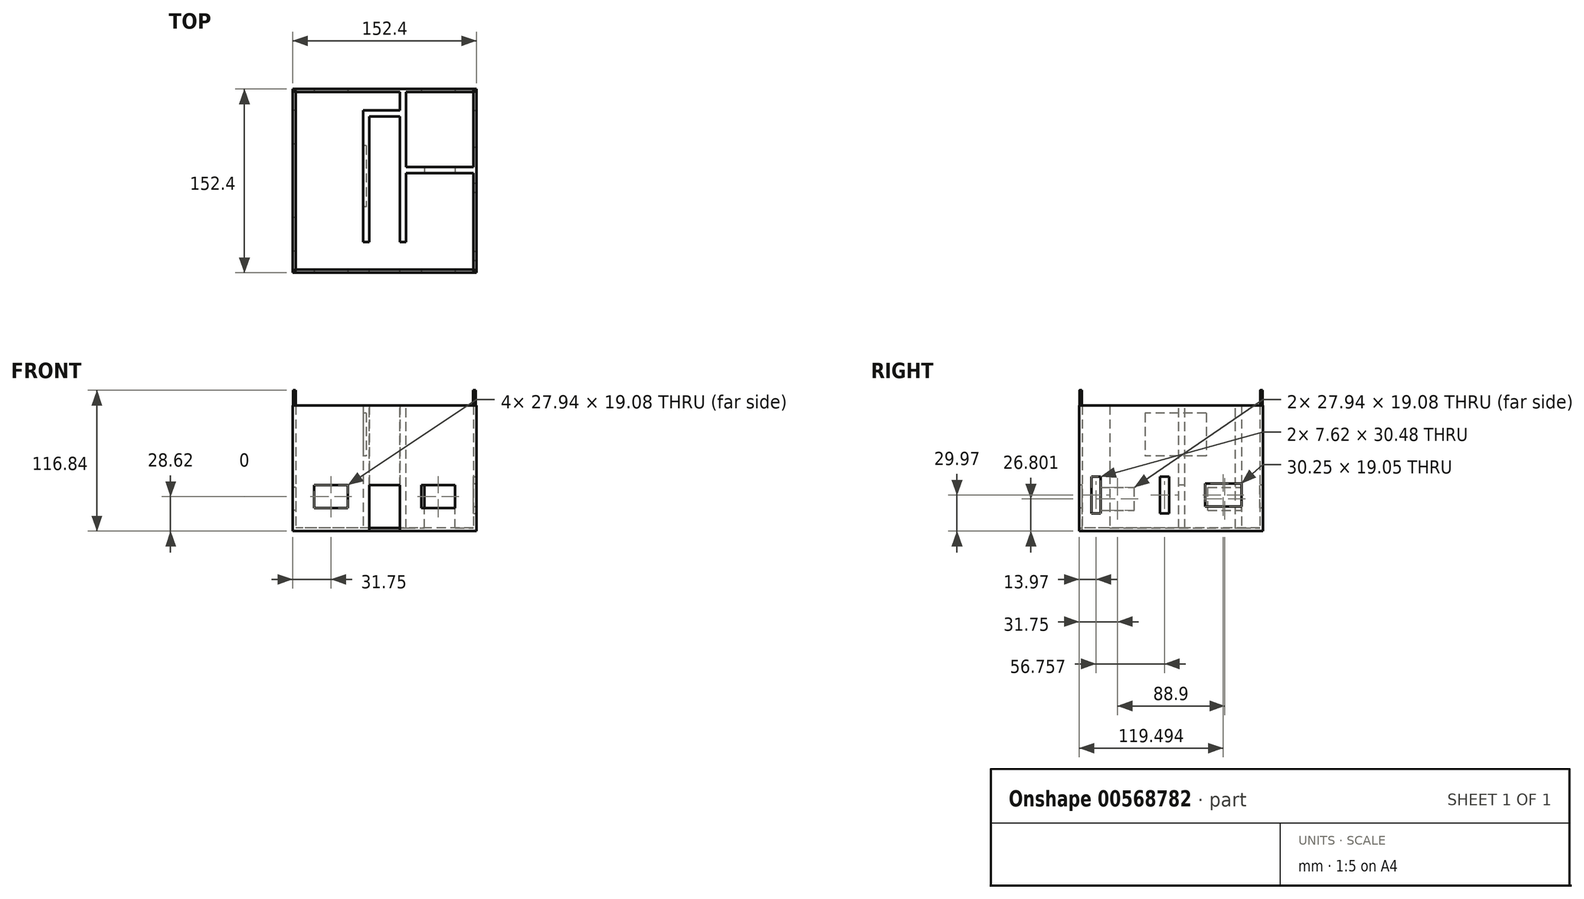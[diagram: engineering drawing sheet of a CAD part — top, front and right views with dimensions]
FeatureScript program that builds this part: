
annotation { "Feature Type Name" : "Feature", "Feature Type Description" : "" }
export const myFeature = defineFeature(function(context is Context, id is Id, definition is map)
    precondition{}
    {
        {
            var Q0;
            Q0=qCreatedBy(makeId("Top.planeOp"),FACE);
            var sketch = newSketch(context, id + "F0", { "sketchPlane" : qUnion([Q0])});
            skLineSegment(sketch, "E0.bottom", {"start": v(0, 0) * mm, "end": v(152.4, 0) * mm});
            skLineSegment(sketch, "E0.top", {"start": v(0, -152.4) * mm, "end": v(152.4, -152.4) * mm});
            skLineSegment(sketch, "E0.left", {"start": v(0, 0) * mm, "end": v(0, -152.4) * mm});
            skLineSegment(sketch, "E0.right", {"start": v(152.4, 0) * mm, "end": v(152.4, -152.4) * mm});
            skSolve(sketch);
        }
        {
            var Q0;
            Q0 = qSketchRegion(id + "F0", true);
            extrude(context, id + "F1", {"entities" : qUnion([Q0]), "depth" : 2.54 * mm, "offsetDistance" : 25.4 * mm});
        }
        {
            var Q0;
            Q0=makeQuery(id+"F1.opExtrude","CAP_FACE",FACE,{"disambiguationData":[OSD([sQuery(id+"F0.wireOp",EDGE,"E0.bottom"),sQuery(id+"F0.wireOp",EDGE,"E0.top"),sQuery(id+"F0.wireOp",EDGE,"E0.left"),sQuery(id+"F0.wireOp",EDGE,"E0.right")])],"isStart":false});
            var sketch = newSketch(context, id + "F2", { "sketchPlane" : qUnion([Q0])});
            skLineSegment(sketch, "E1", {"start": v(76.2, 0) * mm, "end": v(76.2, -152.4) * mm, "construction": true});
            skLineSegment(sketch, "E2", {"start": v(76.2, -152.4) * mm, "end": v(0, -76.2) * mm, "construction": true});
            skLineSegment(sketch, "E3", {"start": v(0, -76.2) * mm, "end": v(152.4, -76.2) * mm, "construction": true});
            skLineSegment(sketch, "E4", {"start": v(152.4, -76.2) * mm, "end": v(76.2, 0) * mm, "construction": true});
            skLineSegment(sketch, "E5.bottom", {"start": v(149.86, -2.54) * mm, "end": v(2.54, -2.54) * mm});
            skLineSegment(sketch, "E5.top", {"start": v(149.86, -149.86) * mm, "end": v(2.54, -149.86) * mm});
            skLineSegment(sketch, "E5.left", {"start": v(149.86, -2.54) * mm, "end": v(149.86, -149.86) * mm});
            skLineSegment(sketch, "E5.right", {"start": v(2.54, -2.54) * mm, "end": v(2.54, -149.86) * mm});
            skSolve(sketch);
        }
        {
            var Q0;
            Q0=makeQuery(id+"F2.imprint","IMPRINT",FACE,{"disambiguationData":[TD([[makeQuery(id+"F2.imprint","IMPRINT",EDGE,{"derivedFrom":sQuery(id+"F2.wireOp",EDGE,"E5.bottom")}),-1.0]])]});
            extrude(context, id + "F3", {"entities" : qUnion([Q0]), "operationType" : NewBodyOperationType.ADD, "depth" : 101.6 * mm, "offsetDistance" : 25.4 * mm});
        }
        {
            var Q0;
            {var subQ0=sQuery(id+"F0.wireOp",EDGE,"E0.top");Q0=makeQuery(id+"F3.boolean.opBoolean","MERGE",FACE,{"derivedFrom":[makeQuery(id+"F1.opExtrude","SWEPT_FACE",FACE,{"disambiguationData":[OSD([subQ0])]}),makeQuery(id+"F3.opExtrude","SWEPT_FACE",FACE,{"disambiguationData":[OSD([subQ0])]})]});}
            var sketch = newSketch(context, id + "F4", { "sketchPlane" : qUnion([Q0])});
            skLineSegment(sketch, "E6", {"start": v(76.2, 104.14) * mm, "end": v(76.2, 0) * mm, "construction": true});
            skLineSegment(sketch, "E7", {"start": v(76.2, 0) * mm, "end": v(0, 52.07) * mm, "construction": true});
            skLineSegment(sketch, "E8", {"start": v(0, 52.07) * mm, "end": v(152.4, 52.07) * mm, "construction": true});
            skLineSegment(sketch, "E9", {"start": v(152.4, 52.07) * mm, "end": v(76.2, 104.14) * mm, "construction": true});
            skLineSegment(sketch, "E10", {"start": v(76.2, 0) * mm, "end": v(88.9, 0) * mm, "construction": true});
            skLineSegment(sketch, "E11", {"start": v(76.2, 0) * mm, "end": v(63.5, 0) * mm, "construction": true});
            skLineSegment(sketch, "E12.bottom", {"start": v(63.5, 0) * mm, "end": v(88.9, 0) * mm});
            skLineSegment(sketch, "E12.top", {"start": v(63.5, 38.16) * mm, "end": v(88.9, 38.16) * mm});
            skLineSegment(sketch, "E12.left", {"start": v(63.5, 0) * mm, "end": v(63.5, 38.16) * mm});
            skLineSegment(sketch, "E12.right", {"start": v(88.9, 0) * mm, "end": v(88.9, 38.16) * mm});
            skSolve(sketch);
        }
        {
            var Q0;
            Q0=makeQuery(id+"F4.imprint","IMPRINT",FACE,{"disambiguationData":[TD([[makeQuery(id+"F4.imprint","IMPRINT",EDGE,{"derivedFrom":sQuery(id+"F4.wireOp",EDGE,"E12.bottom")}),1.0]])]});
            extrude(context, id + "F5", {"entities" : qUnion([Q0]), "operationType" : NewBodyOperationType.REMOVE, "oppositeDirection" : true, "depth" : 25.4 * mm, "offsetDistance" : 25.4 * mm});
        }
        {
            var Q0;
            Q0=makeQuery(id+"F1.opExtrude","CAP_FACE",FACE,{"disambiguationData":[OSD([sQuery(id+"F0.wireOp",EDGE,"E0.bottom"),sQuery(id+"F0.wireOp",EDGE,"E0.top"),sQuery(id+"F0.wireOp",EDGE,"E0.left"),sQuery(id+"F0.wireOp",EDGE,"E0.right")])],"isStart":false});
            var sketch = newSketch(context, id + "F6", { "sketchPlane" : qUnion([Q0])});
            skLineSegment(sketch, "E13.bottom", {"start": v(63.5, -127) * mm, "end": v(88.9, -127) * mm});
            skLineSegment(sketch, "E13.top", {"start": v(63.5, -149.86) * mm, "end": v(88.9, -149.86) * mm});
            skLineSegment(sketch, "E13.left", {"start": v(63.5, -127) * mm, "end": v(63.5, -149.86) * mm});
            skLineSegment(sketch, "E13.right", {"start": v(88.9, -127) * mm, "end": v(88.9, -149.86) * mm});
            skSolve(sketch);
        }
        {
            var Q0;
            Q0 = qSketchRegion(id + "F6", true);
            extrude(context, id + "F7", {"entities" : qUnion([Q0]), "oppositeDirection" : true, "depth" : 2.54 * mm, "offsetDistance" : 25.4 * mm});
        }
        {
            var Q0;
            Q0=makeQuery(id+"F7.opExtrude","SWEPT_FACE",FACE,{"disambiguationData":[OSD([sQuery(id+"F6.wireOp",EDGE,"E13.top")])]});
            var sketch = newSketch(context, id + "F8", { "sketchPlane" : qUnion([Q0])});
            skLineSegment(sketch, "E14.bottom", {"start": v(88.9, 0) * mm, "end": v(63.5, 0) * mm});
            skLineSegment(sketch, "E14.top", {"start": v(88.9, 2.54) * mm, "end": v(63.5, 2.54) * mm});
            skLineSegment(sketch, "E14.left", {"start": v(88.9, 0) * mm, "end": v(88.9, 2.54) * mm});
            skLineSegment(sketch, "E14.right", {"start": v(63.5, 0) * mm, "end": v(63.5, 2.54) * mm});
            skSolve(sketch);
        }
        {
            var Q0;
            Q0 = qSketchRegion(id + "F8", true);
            extrude(context, id + "F9", {"entities" : qUnion([Q0]), "depth" : 2.54 * mm, "offsetDistance" : 25.4 * mm});
        }
        {
            var Q0;
            Q0=makeQuery(id+"F1.opExtrude","CAP_FACE",FACE,{"disambiguationData":[OSD([sQuery(id+"F0.wireOp",EDGE,"E0.bottom"),sQuery(id+"F0.wireOp",EDGE,"E0.top"),sQuery(id+"F0.wireOp",EDGE,"E0.left"),sQuery(id+"F0.wireOp",EDGE,"E0.right")])],"isStart":false});
            var sketch = newSketch(context, id + "F10", { "sketchPlane" : qUnion([Q0])});
            skLineSegment(sketch, "E15.bottom", {"start": v(63.5, -127) * mm, "end": v(58.42, -127) * mm});
            skLineSegment(sketch, "E15.top", {"start": v(63.5, -17.78) * mm, "end": v(58.42, -17.78) * mm});
            skLineSegment(sketch, "E15.left", {"start": v(63.5, -127) * mm, "end": v(63.5, -17.78) * mm});
            skLineSegment(sketch, "E15.right", {"start": v(58.42, -127) * mm, "end": v(58.42, -17.78) * mm});
            skSolve(sketch);
        }
        {
            var Q0;
            Q0=makeQuery(id+"F10.imprint","IMPRINT",FACE,{"disambiguationData":[TD([[makeQuery(id+"F10.imprint","IMPRINT",EDGE,{"derivedFrom":sQuery(id+"F10.wireOp",EDGE,"E15.bottom")}),1.0]])]});
            var sketch = newSketch(context, id + "F11", { "sketchPlane" : qUnion([Q0])});
            skLineSegment(sketch, "E16.0.0", {"start": v(63.5, -127) * mm, "end": v(63.5, -17.78) * mm});
            skLineSegment(sketch, "E16.0.1", {"start": v(63.5, -17.78) * mm, "end": v(58.42, -17.78) * mm});
            skLineSegment(sketch, "E16.0.2", {"start": v(58.42, -17.78) * mm, "end": v(58.42, -127) * mm});
            skLineSegment(sketch, "E16.0.3", {"start": v(58.42, -127) * mm, "end": v(63.5, -127) * mm});
            skLineSegment(sketch, "E17.bottom", {"start": v(88.9, -127) * mm, "end": v(93.98, -127) * mm});
            skLineSegment(sketch, "E17.top", {"start": v(88.9, -2.54) * mm, "end": v(93.98, -2.54) * mm});
            skLineSegment(sketch, "E17.left", {"start": v(88.9, -127) * mm, "end": v(88.9, -2.54) * mm});
            skLineSegment(sketch, "E17.right", {"start": v(93.98, -127) * mm, "end": v(93.98, -2.54) * mm});
            skSolve(sketch);
        }
        {
            var Q0;
            Q0 = qSketchRegion(id + "F11", true);
            extrude(context, id + "F12", {"entities" : qUnion([Q0]), "operationType" : NewBodyOperationType.ADD, "depth" : 101.6 * mm, "offsetDistance" : 25.4 * mm});
        }
        {
            var Q0;
            Q0=makeQuery(id+"F12.opExtrude","CAP_FACE",FACE,{"disambiguationData":[OSD([sQuery(id+"F11.wireOp",EDGE,"E16.0.0"),sQuery(id+"F11.wireOp",EDGE,"E16.0.1"),sQuery(id+"F11.wireOp",EDGE,"E16.0.2"),sQuery(id+"F11.wireOp",EDGE,"E16.0.3")])],"isStart":false});
            var sketch = newSketch(context, id + "F13", { "sketchPlane" : qUnion([Q0])});
            skLineSegment(sketch, "E18.bottom", {"start": v(63.5, -17.78) * mm, "end": v(88.9, -17.78) * mm});
            skLineSegment(sketch, "E18.top", {"start": v(63.5, -22.86) * mm, "end": v(88.9, -22.86) * mm});
            skLineSegment(sketch, "E18.left", {"start": v(63.5, -17.78) * mm, "end": v(63.5, -22.86) * mm});
            skLineSegment(sketch, "E18.right", {"start": v(88.9, -17.78) * mm, "end": v(88.9, -22.86) * mm});
            skSolve(sketch);
        }
        {
            var Q0;
            Q0 = qSketchRegion(id + "F13", true);
            extrude(context, id + "F14", {"entities" : qUnion([Q0]), "operationType" : NewBodyOperationType.ADD, "oppositeDirection" : true, "depth" : 101.6 * mm, "offsetDistance" : 25.4 * mm});
        }
        {
            var Q0;
            Q0=makeQuery(id+"F12.opExtrude","SWEPT_FACE",FACE,{"disambiguationData":[OSD([sQuery(id+"F11.wireOp",EDGE,"E16.0.2")])]});
            var sketch = newSketch(context, id + "F15", { "sketchPlane" : qUnion([Q0])});
            skLineSegment(sketch, "E19.bottom", {"start": v(97.79, 62.39) * mm, "end": v(46.99, 62.39) * mm, "construction": true});
            skLineSegment(sketch, "E19.top", {"start": v(97.79, 97.95) * mm, "end": v(46.99, 97.95) * mm, "construction": true});
            skLineSegment(sketch, "E19.left", {"start": v(97.79, 62.39) * mm, "end": v(97.79, 97.95) * mm, "construction": true});
            skLineSegment(sketch, "E19.right", {"start": v(46.99, 62.39) * mm, "end": v(46.99, 97.95) * mm, "construction": true});
            skPoint(sketch, "E19.middle", {"position": v(72.39, 80.17) * mm});
            skLineSegment(sketch, "E20.bottom", {"start": v(46.99, 97.95) * mm, "end": v(97.79, 97.95) * mm});
            skLineSegment(sketch, "E20.top", {"start": v(46.99, 62.39) * mm, "end": v(97.79, 62.39) * mm});
            skLineSegment(sketch, "E20.left", {"start": v(46.99, 97.95) * mm, "end": v(46.99, 62.39) * mm});
            skLineSegment(sketch, "E20.right", {"start": v(97.79, 97.95) * mm, "end": v(97.79, 62.39) * mm});
            skSolve(sketch);
        }
        {
            var Q0;
            Q0 = qSketchRegion(id + "F15", true);
            extrude(context, id + "F16", {"entities" : qUnion([Q0]), "operationType" : NewBodyOperationType.REMOVE, "oppositeDirection" : true, "depth" : 2.54 * mm, "offsetDistance" : 25.4 * mm});
        }
        {
            var Q0;
            Q0=makeQuery(id+"F14.boolean.opBoolean","MERGE",FACE,{"derivedFrom":[makeQuery(id+"F12.opExtrude","CAP_FACE",FACE,{"disambiguationData":[OSD([sQuery(id+"F11.wireOp",EDGE,"E16.0.0"),sQuery(id+"F11.wireOp",EDGE,"E16.0.1"),sQuery(id+"F11.wireOp",EDGE,"E16.0.2"),sQuery(id+"F11.wireOp",EDGE,"E16.0.3")])],"isStart":false}),makeQuery(id+"F12.boolean.opBoolean","MERGE",FACE,{"derivedFrom":[makeQuery(id+"F3.opExtrude","CAP_FACE",FACE,{"disambiguationData":[OSD([sQuery(id+"F0.wireOp",EDGE,"E0.bottom"),sQuery(id+"F0.wireOp",EDGE,"E0.top"),sQuery(id+"F0.wireOp",EDGE,"E0.left"),sQuery(id+"F0.wireOp",EDGE,"E0.right"),sQuery(id+"F2.wireOp",EDGE,"E5.bottom"),sQuery(id+"F2.wireOp",EDGE,"E5.top"),sQuery(id+"F2.wireOp",EDGE,"E5.left"),sQuery(id+"F2.wireOp",EDGE,"E5.right")])],"isStart":false}),makeQuery(id+"F12.opExtrude","CAP_FACE",FACE,{"disambiguationData":[OSD([sQuery(id+"F11.wireOp",EDGE,"E17.bottom"),sQuery(id+"F11.wireOp",EDGE,"E17.top"),sQuery(id+"F11.wireOp",EDGE,"E17.left"),sQuery(id+"F11.wireOp",EDGE,"E17.right")])],"isStart":false})]}),makeQuery(id+"F14.opExtrude","CAP_FACE",FACE,{"disambiguationData":[OSD([sQuery(id+"F13.wireOp",EDGE,"E18.bottom"),sQuery(id+"F13.wireOp",EDGE,"E18.top"),sQuery(id+"F13.wireOp",EDGE,"E18.left"),sQuery(id+"F13.wireOp",EDGE,"E18.right")])],"isStart":true})]});
            var sketch = newSketch(context, id + "F17", { "sketchPlane" : qUnion([Q0])});
            skLineSegment(sketch, "E21.bottom", {"start": v(93.98, -64.77) * mm, "end": v(149.86, -64.77) * mm});
            skLineSegment(sketch, "E21.top", {"start": v(93.98, -69.85) * mm, "end": v(149.86, -69.85) * mm});
            skLineSegment(sketch, "E21.left", {"start": v(93.98, -64.77) * mm, "end": v(93.98, -69.85) * mm});
            skLineSegment(sketch, "E21.right", {"start": v(149.86, -64.77) * mm, "end": v(149.86, -69.85) * mm});
            skSolve(sketch);
        }
        {
            var Q0;
            Q0 = qSketchRegion(id + "F17", true);
            extrude(context, id + "F18", {"entities" : qUnion([Q0]), "operationType" : NewBodyOperationType.ADD, "oppositeDirection" : true, "depth" : 101.6 * mm, "offsetDistance" : 25.4 * mm});
        }
        {
            var Q0;
            Q0=makeQuery(id+"F18.opExtrude","SWEPT_FACE",FACE,{"disambiguationData":[OSD([sQuery(id+"F17.wireOp",EDGE,"E21.top")])]});
            var sketch = newSketch(context, id + "F19", { "sketchPlane" : qUnion([Q0])});
            skLineSegment(sketch, "E22", {"start": v(69.35, -89.43) * mm, "end": v(69.35, -53.96) * mm});
            skLineSegment(sketch, "E23", {"start": v(121.92, 2.54) * mm, "end": v(121.92, 104.14) * mm, "construction": true});
            skLineSegment(sketch, "E24", {"start": v(121.92, 104.14) * mm, "end": v(149.86, 53.34) * mm, "construction": true});
            skLineSegment(sketch, "E25", {"start": v(149.86, 53.34) * mm, "end": v(93.98, 53.34) * mm, "construction": true});
            skLineSegment(sketch, "E26", {"start": v(121.92, 2.54) * mm, "end": v(109.22, 2.54) * mm});
            skLineSegment(sketch, "E27", {"start": v(121.92, 2.54) * mm, "end": v(134.62, 2.54) * mm});
            skLineSegment(sketch, "E28.bottom", {"start": v(109.22, 2.54) * mm, "end": v(134.62, 2.54) * mm});
            skLineSegment(sketch, "E28.top", {"start": v(109.22, 38.1) * mm, "end": v(134.62, 38.1) * mm});
            skLineSegment(sketch, "E28.left", {"start": v(109.22, 2.54) * mm, "end": v(109.22, 38.1) * mm});
            skLineSegment(sketch, "E28.right", {"start": v(134.62, 2.54) * mm, "end": v(134.62, 38.1) * mm});
            skSolve(sketch);
        }
        {
            var Q0;
            Q0 = qSketchRegion(id + "F19", true);
            extrude(context, id + "F20", {"entities" : qUnion([Q0]), "operationType" : NewBodyOperationType.REMOVE, "oppositeDirection" : true, "depth" : 5.08 * mm, "offsetDistance" : 25.4 * mm});
        }
        {
            var Q0;
            {var subQ0=sQuery(id+"F0.wireOp",EDGE,"E0.top");Q0=makeQuery(id+"F3.boolean.opBoolean","MERGE",FACE,{"derivedFrom":[makeQuery(id+"F1.opExtrude","SWEPT_FACE",FACE,{"disambiguationData":[OSD([subQ0])]}),makeQuery(id+"F3.opExtrude","SWEPT_FACE",FACE,{"disambiguationData":[OSD([subQ0])]})]});}
            var sketch = newSketch(context, id + "F21", { "sketchPlane" : qUnion([Q0])});
            skPoint(sketch, "E29.endSnap0", {"position": v(0, 52.07) * mm});
            skLineSegment(sketch, "E30", {"start": v(106.68, 19.08) * mm, "end": v(106.68, 38.16) * mm});
            skLineSegment(sketch, "E31", {"start": v(106.68, 38.16) * mm, "end": v(134.62, 38.16) * mm});
            skLineSegment(sketch, "E32", {"start": v(134.62, 38.16) * mm, "end": v(134.62, 19.08) * mm});
            skLineSegment(sketch, "E33", {"start": v(134.62, 19.08) * mm, "end": v(106.68, 19.08) * mm});
            skLineSegment(sketch, "E34.bottom", {"start": v(17.78, 19.08) * mm, "end": v(45.72, 19.08) * mm});
            skLineSegment(sketch, "E34.top", {"start": v(17.78, 38.16) * mm, "end": v(45.72, 38.16) * mm});
            skLineSegment(sketch, "E34.left", {"start": v(17.78, 19.08) * mm, "end": v(17.78, 38.16) * mm});
            skLineSegment(sketch, "E34.right", {"start": v(45.72, 19.08) * mm, "end": v(45.72, 38.16) * mm});
            skLineSegment(sketch, "E35", {"start": v(0, 52.07) * mm, "end": v(152.4, 52.07) * mm});
            skLineSegment(sketch, "E36.MirrorCS", {"start": v(17.78, 65.98) * mm, "end": v(45.72, 65.98) * mm});
            skLineSegment(sketch, "E37.MirrorCS", {"start": v(17.78, 85.06) * mm, "end": v(17.78, 65.98) * mm});
            skLineSegment(sketch, "E38.MirrorCS", {"start": v(45.72, 85.06) * mm, "end": v(45.72, 65.98) * mm});
            skLineSegment(sketch, "E39.MirrorCS", {"start": v(17.78, 85.06) * mm, "end": v(45.72, 85.06) * mm});
            skLineSegment(sketch, "E40.MirrorCS", {"start": v(106.68, 85.06) * mm, "end": v(106.68, 65.98) * mm});
            skLineSegment(sketch, "E41.MirrorCS", {"start": v(106.68, 65.98) * mm, "end": v(134.62, 65.98) * mm});
            skLineSegment(sketch, "E42.MirrorCS", {"start": v(134.62, 65.98) * mm, "end": v(134.62, 85.06) * mm});
            skLineSegment(sketch, "E43.MirrorCS", {"start": v(134.62, 85.06) * mm, "end": v(106.68, 85.06) * mm});
            skSolve(sketch);
        }
        {
            var Q0;
            {var subQ0=sQuery(id+"F0.wireOp",EDGE,"E0.right");Q0=makeQuery(id+"F3.boolean.opBoolean","MERGE",FACE,{"derivedFrom":[makeQuery(id+"F1.opExtrude","SWEPT_FACE",FACE,{"disambiguationData":[OSD([subQ0])]}),makeQuery(id+"F3.opExtrude","SWEPT_FACE",FACE,{"disambiguationData":[OSD([subQ0])]})]});}
            var sketch = newSketch(context, id + "F22", { "sketchPlane" : qUnion([Q0])});
            skLineSegment(sketch, "E44", {"start": v(-67.7, 106.68) * mm, "end": v(-67.7, 104.14) * mm});
            skLineSegment(sketch, "E45", {"start": v(-67.7, 104.14) * mm, "end": v(-67.7, 0) * mm});
            skLineSegment(sketch, "E46", {"start": v(-67.7, 52.07) * mm, "end": v(-152.4, 52.07) * mm, "construction": true});
            skLineSegment(sketch, "E47.bottom", {"start": v(-134.62, 14.73) * mm, "end": v(-142.24, 14.73) * mm});
            skLineSegment(sketch, "E47.top", {"start": v(-134.62, 45.2) * mm, "end": v(-142.24, 45.2) * mm});
            skLineSegment(sketch, "E47.left", {"start": v(-134.62, 14.73) * mm, "end": v(-134.62, 45.2) * mm});
            skLineSegment(sketch, "E47.right", {"start": v(-142.24, 14.73) * mm, "end": v(-142.24, 45.2) * mm});
            skPoint(sketch, "E47.middle", {"position": v(-138.43, 29.97) * mm});
            skLineSegment(sketch, "E48.bottom", {"start": v(-77.86, 14.73) * mm, "end": v(-85.48, 14.73) * mm});
            skLineSegment(sketch, "E48.top", {"start": v(-77.86, 45.2) * mm, "end": v(-85.48, 45.2) * mm});
            skLineSegment(sketch, "E48.left", {"start": v(-77.86, 14.73) * mm, "end": v(-77.86, 45.2) * mm});
            skLineSegment(sketch, "E48.right", {"start": v(-85.48, 14.73) * mm, "end": v(-85.48, 45.2) * mm});
            skPoint(sketch, "E48.middle", {"position": v(-81.67, 29.97) * mm});
            skSolve(sketch);
        }
        {
            var Q0;
            Q0=makeQuery(id+"F22.imprint","IMPRINT",FACE,{"disambiguationData":[TD([[makeQuery(id+"F22.imprint","IMPRINT",EDGE,{"derivedFrom":sQuery(id+"F22.wireOp",EDGE,"E47.bottom")}),-1.0]])]});
            var Q1;
            Q1=makeQuery(id+"F22.imprint","IMPRINT",FACE,{"disambiguationData":[TD([[makeQuery(id+"F22.imprint","IMPRINT",EDGE,{"derivedFrom":sQuery(id+"F22.wireOp",EDGE,"E48.bottom")}),-1.0]])]});
            extrude(context, id + "F23", {"entities" : qUnion([Q0, Q1]), "operationType" : NewBodyOperationType.REMOVE, "oppositeDirection" : true, "depth" : 25.4 * mm, "offsetDistance" : 25.4 * mm});
        }
        {
            var Q0;
            {var subQ0=sQuery(id+"F0.wireOp",EDGE,"E0.right");Q0=makeQuery(id+"F3.boolean.opBoolean","MERGE",FACE,{"derivedFrom":[makeQuery(id+"F1.opExtrude","SWEPT_FACE",FACE,{"disambiguationData":[OSD([subQ0])]}),makeQuery(id+"F3.opExtrude","SWEPT_FACE",FACE,{"disambiguationData":[OSD([subQ0])]})]});}
            var sketch = newSketch(context, id + "F24", { "sketchPlane" : qUnion([Q0])});
            skLineSegment(sketch, "E49.bottom", {"start": v(-17.78, 20.44) * mm, "end": v(-48.03, 20.44) * mm});
            skLineSegment(sketch, "E49.top", {"start": v(-17.78, 39.5) * mm, "end": v(-48.03, 39.5) * mm});
            skLineSegment(sketch, "E49.left", {"start": v(-17.78, 20.44) * mm, "end": v(-17.78, 39.5) * mm});
            skLineSegment(sketch, "E49.right", {"start": v(-48.03, 20.44) * mm, "end": v(-48.03, 39.5) * mm});
            skPoint(sketch, "E49.middle", {"position": v(-32.9, 29.97) * mm});
            skPoint(sketch, "E49.middle.positionSnap0", {"position": v(-77.86, 29.97) * mm});
            skPoint(sketch, "E49.centerSnap0", {"position": v(-77.86, 29.97) * mm});
            skSolve(sketch);
        }
        {
            var Q0;
            Q0=makeQuery(id+"F24.imprint","IMPRINT",FACE,{"disambiguationData":[TD([[makeQuery(id+"F24.imprint","IMPRINT",EDGE,{"derivedFrom":sQuery(id+"F24.wireOp",EDGE,"E49.bottom")}),-1.0]])]});
            extrude(context, id + "F25", {"entities" : qUnion([Q0]), "operationType" : NewBodyOperationType.REMOVE, "oppositeDirection" : true, "depth" : 25.4 * mm, "offsetDistance" : 25.4 * mm});
        }
        {
            var Q0;
            Q0=makeQuery(id+"F21.imprint","IMPRINT",FACE,{"disambiguationData":[TD([[makeQuery(id+"F21.imprint","IMPRINT",EDGE,{"derivedFrom":sQuery(id+"F21.wireOp",EDGE,"E34.bottom")}),1.0]])]});
            extrude(context, id + "F26", {"entities" : qUnion([Q0]), "operationType" : NewBodyOperationType.REMOVE, "oppositeDirection" : true, "depth" : 254 * mm, "offsetDistance" : 25.4 * mm});
        }
        {
            var Q0;
            Q0=makeQuery(id+"F21.imprint","IMPRINT",FACE,{"disambiguationData":[TD([[makeQuery(id+"F21.imprint","IMPRINT",EDGE,{"derivedFrom":sQuery(id+"F21.wireOp",EDGE,"E30")}),-1.0]])]});
            extrude(context, id + "F27", {"entities" : qUnion([Q0]), "operationType" : NewBodyOperationType.REMOVE, "oppositeDirection" : true, "depth" : 254 * mm, "offsetDistance" : 25.4 * mm});
        }
        {
            var Q0;
            Q0=makeQuery(id+"F27.boolean.opBoolean","COPY",FACE,{"disambiguationData":[TD([makeQuery(id+"F18.opExtrude","SWEPT_FACE",FACE,{"disambiguationData":[OSD([sQuery(id+"F17.wireOp",EDGE,"E21.bottom")])]})])],"derivedFrom":makeQuery(id+"F27.opExtrude","SWEPT_FACE",FACE,{"disambiguationData":[OSD([sQuery(id+"F21.wireOp",EDGE,"E33")])]})});
            var sketch = newSketch(context, id + "F28", { "sketchPlane" : qUnion([Q0])});
            skLineSegment(sketch, "E50.bottom", {"start": v(106.68, -69.85) * mm, "end": v(109.22, -69.85) * mm});
            skLineSegment(sketch, "E50.top", {"start": v(106.68, -64.77) * mm, "end": v(109.22, -64.77) * mm});
            skLineSegment(sketch, "E50.left", {"start": v(106.68, -69.85) * mm, "end": v(106.68, -64.77) * mm});
            skLineSegment(sketch, "E50.right", {"start": v(109.22, -69.85) * mm, "end": v(109.22, -64.77) * mm});
            skSolve(sketch);
        }
        {
            var Q0;
            Q0 = qSketchRegion(id + "F28", true);
            extrude(context, id + "F29", {"entities" : qUnion([Q0]), "operationType" : NewBodyOperationType.ADD, "depth" : 25.4 * mm, "offsetDistance" : 25.4 * mm});
        }
        {
            var Q0;
            {var subQ0=sQuery(id+"F0.wireOp",EDGE,"E0.left");Q0=makeQuery(id+"F3.boolean.opBoolean","MERGE",FACE,{"derivedFrom":[makeQuery(id+"F1.opExtrude","SWEPT_FACE",FACE,{"disambiguationData":[OSD([subQ0])]}),makeQuery(id+"F3.opExtrude","SWEPT_FACE",FACE,{"disambiguationData":[OSD([subQ0])]})]});}
            var sketch = newSketch(context, id + "F30", { "sketchPlane" : qUnion([Q0])});
            skLineSegment(sketch, "E51", {"start": v(152.4, 26.8) * mm, "end": v(0, 26.8) * mm, "construction": true});
            skLineSegment(sketch, "E52.bottom", {"start": v(134.62, 17.26) * mm, "end": v(106.68, 17.26) * mm});
            skLineSegment(sketch, "E52.top", {"start": v(134.62, 36.34) * mm, "end": v(106.68, 36.34) * mm});
            skLineSegment(sketch, "E52.left", {"start": v(134.62, 17.26) * mm, "end": v(134.62, 36.34) * mm});
            skLineSegment(sketch, "E52.right", {"start": v(106.68, 17.26) * mm, "end": v(106.68, 36.34) * mm});
            skPoint(sketch, "E52.middle", {"position": v(120.65, 26.8) * mm});
            skLineSegment(sketch, "E53.bottom", {"start": v(45.72, 17.26) * mm, "end": v(17.78, 17.26) * mm});
            skLineSegment(sketch, "E53.top", {"start": v(45.72, 36.34) * mm, "end": v(17.78, 36.34) * mm});
            skLineSegment(sketch, "E53.left", {"start": v(45.72, 17.26) * mm, "end": v(45.72, 36.34) * mm});
            skLineSegment(sketch, "E53.right", {"start": v(17.78, 17.26) * mm, "end": v(17.78, 36.34) * mm});
            skPoint(sketch, "E53.middle", {"position": v(31.75, 26.8) * mm});
            skSolve(sketch);
        }
        {
            var Q0;
            Q0 = qSketchRegion(id + "F30", true);
            extrude(context, id + "F31", {"entities" : qUnion([Q0]), "operationType" : NewBodyOperationType.REMOVE, "oppositeDirection" : true, "depth" : 25.4 * mm, "offsetDistance" : 25.4 * mm});
        }
        {
            var Q0;
            Q0=makeQuery(id+"F18.boolean.opBoolean","MERGE",FACE,{"derivedFrom":[makeQuery(id+"F14.boolean.opBoolean","MERGE",FACE,{"derivedFrom":[makeQuery(id+"F12.opExtrude","CAP_FACE",FACE,{"disambiguationData":[OSD([sQuery(id+"F11.wireOp",EDGE,"E16.0.0"),sQuery(id+"F11.wireOp",EDGE,"E16.0.1"),sQuery(id+"F11.wireOp",EDGE,"E16.0.2"),sQuery(id+"F11.wireOp",EDGE,"E16.0.3")])],"isStart":false}),makeQuery(id+"F12.boolean.opBoolean","MERGE",FACE,{"derivedFrom":[makeQuery(id+"F3.opExtrude","CAP_FACE",FACE,{"disambiguationData":[OSD([sQuery(id+"F0.wireOp",EDGE,"E0.bottom"),sQuery(id+"F0.wireOp",EDGE,"E0.top"),sQuery(id+"F0.wireOp",EDGE,"E0.left"),sQuery(id+"F0.wireOp",EDGE,"E0.right"),sQuery(id+"F2.wireOp",EDGE,"E5.bottom"),sQuery(id+"F2.wireOp",EDGE,"E5.top"),sQuery(id+"F2.wireOp",EDGE,"E5.left"),sQuery(id+"F2.wireOp",EDGE,"E5.right")])],"isStart":false}),makeQuery(id+"F12.opExtrude","CAP_FACE",FACE,{"disambiguationData":[OSD([sQuery(id+"F11.wireOp",EDGE,"E17.bottom"),sQuery(id+"F11.wireOp",EDGE,"E17.top"),sQuery(id+"F11.wireOp",EDGE,"E17.left"),sQuery(id+"F11.wireOp",EDGE,"E17.right")])],"isStart":false})]}),makeQuery(id+"F14.opExtrude","CAP_FACE",FACE,{"disambiguationData":[OSD([sQuery(id+"F13.wireOp",EDGE,"E18.bottom"),sQuery(id+"F13.wireOp",EDGE,"E18.top"),sQuery(id+"F13.wireOp",EDGE,"E18.left"),sQuery(id+"F13.wireOp",EDGE,"E18.right")])],"isStart":true})]}),makeQuery(id+"F18.opExtrude","CAP_FACE",FACE,{"disambiguationData":[OSD([sQuery(id+"F17.wireOp",EDGE,"E21.bottom"),sQuery(id+"F17.wireOp",EDGE,"E21.top"),sQuery(id+"F17.wireOp",EDGE,"E21.left"),sQuery(id+"F17.wireOp",EDGE,"E21.right")])],"isStart":true})]});
            var sketch = newSketch(context, id + "F32", { "sketchPlane" : qUnion([Q0])});
            skLineSegment(sketch, "E54.bottom", {"start": v(0, 0) * mm, "end": v(152.4, 0) * mm});
            skLineSegment(sketch, "E54.top", {"start": v(0, -152.4) * mm, "end": v(152.4, -152.4) * mm});
            skLineSegment(sketch, "E54.left", {"start": v(0, 0) * mm, "end": v(0, -152.4) * mm});
            skLineSegment(sketch, "E54.right", {"start": v(152.4, 0) * mm, "end": v(152.4, -152.4) * mm});
            skSolve(sketch);
        }
        {
            var Q0;
            Q0=makeQuery(id+"F32.imprint","IMPRINT",FACE,{"disambiguationData":[TD([[makeQuery(id+"F32.imprint","IMPRINT",EDGE,{"derivedFrom":sQuery(id+"F32.wireOp",EDGE,"E54.bottom")}),-1.0]])]});
            var sketch = newSketch(context, id + "F33", { "sketchPlane" : qUnion([Q0])});
            skLineSegment(sketch, "E55.bottom", {"start": v(58.42, -17.78) * mm, "end": v(93.98, -17.78) * mm});
            skLineSegment(sketch, "E55.top", {"start": v(58.42, -127) * mm, "end": v(93.98, -127) * mm});
            skLineSegment(sketch, "E55.left", {"start": v(58.42, -17.78) * mm, "end": v(58.42, -127) * mm});
            skLineSegment(sketch, "E55.right", {"start": v(93.98, -17.78) * mm, "end": v(93.98, -127) * mm});
            skLineSegment(sketch, "E56", {"start": v(58.42, -127) * mm, "end": v(58.42, -149.86) * mm});
            skLineSegment(sketch, "E57.bottom", {"start": v(63.5, -22.86) * mm, "end": v(88.9, -22.86) * mm});
            skLineSegment(sketch, "E57.top", {"start": v(63.5, -127) * mm, "end": v(88.9, -127) * mm});
            skLineSegment(sketch, "E57.left", {"start": v(63.5, -22.86) * mm, "end": v(63.5, -127) * mm});
            skLineSegment(sketch, "E57.right", {"start": v(88.9, -22.86) * mm, "end": v(88.9, -127) * mm});
            skSolve(sketch);
        }
        {
            var Q0;
            Q0=makeQuery(id+"F33.imprint","IMPRINT",FACE,{"disambiguationData":[TD([[makeQuery(id+"F33.imprint","IMPRINT",EDGE,{"derivedFrom":makeQuery(id+"F32.imprint","IMPRINT",EDGE,{"derivedFrom":sQuery(id+"F32.wireOp",EDGE,"E54.bottom")})}),-1.0]])]});
            var sketch = newSketch(context, id + "F34", { "sketchPlane" : qUnion([Q0])});
            skCircle(sketch, "E58", {"center": v(1.23, -151.13) * mm, "radius": 1.02 * mm});
            skCircle(sketch, "E59", {"center": v(1.34, -1.27) * mm, "radius": 1.02 * mm});
            skCircle(sketch, "E60", {"center": v(150.74, -1.27) * mm, "radius": 1.02 * mm});
            skCircle(sketch, "E61", {"center": v(150.69, -151.13) * mm, "radius": 1.02 * mm});
            skSolve(sketch);
        }
        {
            var Q0;
            Q0 = qSketchRegion(id + "F34", true);
            extrude(context, id + "F35", {"entities" : qUnion([Q0]), "operationType" : NewBodyOperationType.ADD, "depth" : 12.7 * mm, "offsetDistance" : 25.4 * mm});
        }
    });
